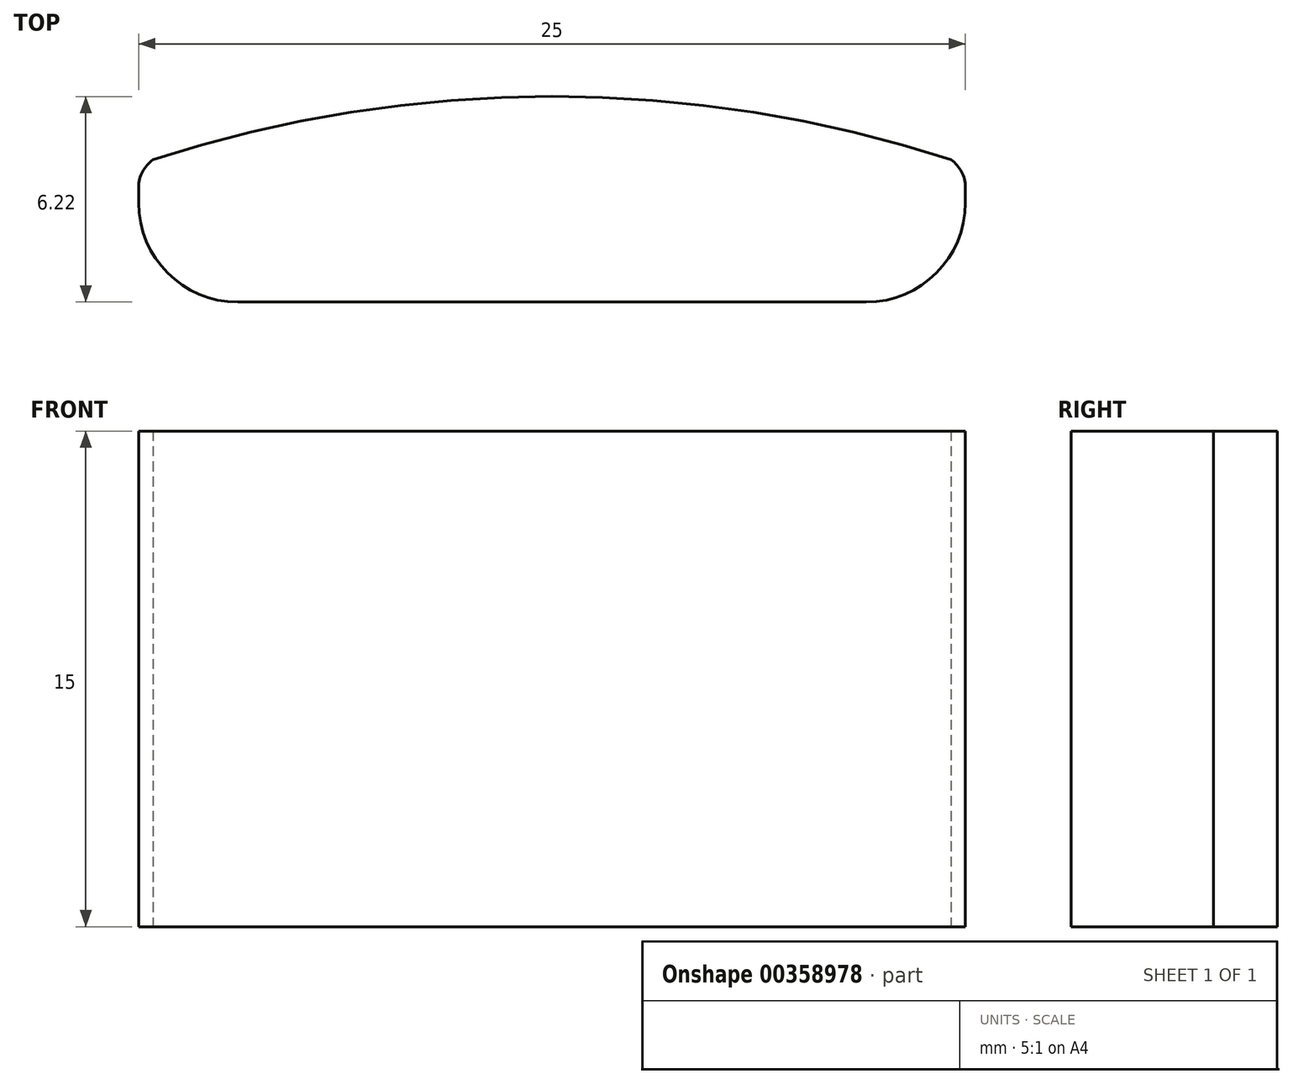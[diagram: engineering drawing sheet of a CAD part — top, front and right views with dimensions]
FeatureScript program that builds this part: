
annotation { "Feature Type Name" : "Feature", "Feature Type Description" : "" }
export const myFeature = defineFeature(function(context is Context, id is Id, definition is map)
    precondition{}
    {
        {
            var Q0;
            Q0=qCreatedBy(makeId("Top.planeOp"),FACE);
            var sketch = newSketch(context, id + "F0", { "sketchPlane" : qUnion([Q0])});
            skLineSegment(sketch, "E0", {"start": v(-18.4, 17.79) * mm, "end": v(0.6, 17.79) * mm});
            skLineSegment(sketch, "E1", {"start": v(3.6, 20.79) * mm, "end": v(3.6, 21.27) * mm});
            skLineSegment(sketch, "E2", {"start": v(-21.4, 20.79) * mm, "end": v(-21.4, 21.27) * mm});
            skPoint(sketch, "E3.visualSharp", {"position": v(-21.4, 17.79) * mm});
            skArc(sketch, "E3.filletArc", {"start": v(-21.4, 20.79) * mm, "mid": v(-20.51, 18.67) * mm, "end": v(-18.4, 17.79) * mm});
            skPoint(sketch, "E4.visualSharp", {"position": v(3.6, 17.79) * mm});
            skArc(sketch, "E4.filletArc", {"start": v(0.6, 17.79) * mm, "mid": v(2.73, 18.67) * mm, "end": v(3.6, 20.79) * mm});
            skPoint(sketch, "E5.visualSharp", {"position": v(3.6, 21.79) * mm});
            skArc(sketch, "E5.filletArc", {"start": v(3.6, 21.27) * mm, "mid": v(3.5, 21.74) * mm, "end": v(3.17, 22.1) * mm});
            skPoint(sketch, "E6.visualSharp", {"position": v(-21.4, 21.79) * mm});
            skArc(sketch, "E6.filletArc", {"start": v(-20.95, 22.1) * mm, "mid": v(-21.28, 21.74) * mm, "end": v(-21.4, 21.27) * mm});
            skArc(sketch, "E7", {"start": v(3.17, 22.1) * mm, "mid": v(-8.9, 24.01) * mm, "end": v(-20.95, 22.1) * mm});
            skSolve(sketch);
        }
        {
            var Q0;
            Q0=makeQuery(id+"F0.imprint","IMPRINT",FACE,{"disambiguationData":[TD([[makeQuery(id+"F0.imprint","IMPRINT",EDGE,{"derivedFrom":sQuery(id+"F0.wireOp",EDGE,"E0")}),1.0]])]});
            extrude(context, id + "F1", {"entities" : qUnion([Q0]), "depth" : 15 * mm});
        }
    });
